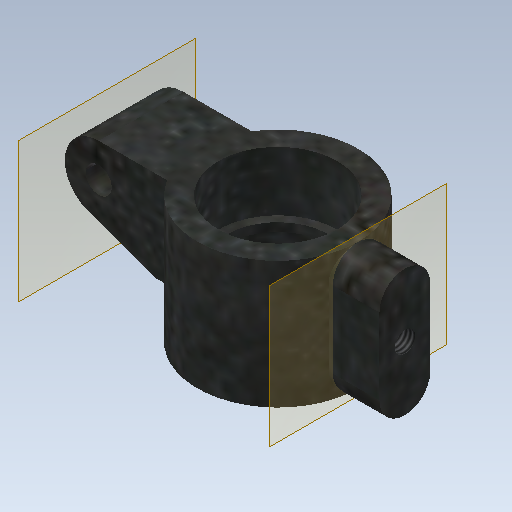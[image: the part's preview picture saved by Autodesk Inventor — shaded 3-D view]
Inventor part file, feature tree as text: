
AUTODESK INVENTOR PART (.ipt)
format: ipt  version: 2020 (Build 240168000, 168)  size: 269,824 bytes
history: native  units: mm
features: sketch x8, extrude x6, hole x3, plane x2, projected_geometry x1
ambient origin geometry x8: Origin, YZ Plane, XZ Plane, XY Plane, X Axis, Y Axis, Z Axis, Center Point
bodies: Solid1 (feature_tree)
feature tree (20):
  extrude  "Extrusion1"  Depth=15.0mm TaperAngle=0.0deg
  extrude  "Extrusion2"  Depth=7.0mm TaperAngle=0.0deg
  extrude  "Extrusion3"  Depth=7.0mm TaperAngle=0.0deg
  extrude  "Extrusion4"  Depth=21.5mm TaperAngle=0.0deg
  plane  "Work Plane1"
  extrude  "Extrusion5"  Depth=5.5mm TaperAngle=0.0deg
  extrude  "Extrusion6"  Depth=4.0mm
  hole  "Hole1"  [1 undecoded]
  hole  "Hole2"  [1 undecoded]
  plane  "Work Plane2"
  hole  "Hole3"  [1 undecoded]
  sketch  "Sketch1"  dims[d0=19.0mm d1=15.0mm d2=0.0mm]
  sketch  "Sketch2"  dims[d3=14.0mm d4=7.0mm d5=0.0mm]
  sketch  "Sketch3"  dims[d6=14.0mm d7=7.0mm d8=0.0mm]
  sketch  "Sketch5"  dims[d9=12.0mm d10=21.5mm d11=0.0mm]
  sketch  "Sketch6"  dims[d13=3.0mm d14=5.5mm d15=0.0mm]
  sketch  "Sketch7"  dims[d16=1.25mm d17=0.0mm d18=4.0mm]
  sketch  "Sketch8"  dims[d19=3.490659mm d21=16.15mm]
  sketch  "Sketch9"  dims[d22=10.0mm d23=0.0mm d49=10.0mm d50=10.0mm d26=3.1mm d27=6.0mm d28=4.0mm d29=2.0mm d30=90.0deg d31=17.3mm d32=20.594885mm d33=2.459mm d34=4.0mm d35=4.0mm d36=2.0mm d37=90.0deg d38=6.0mm d39=20.594885mm d40=2.459mm d41=4.0mm d42=4.0mm d43=2.0mm d44=90.0deg d45=4.0mm d46=20.594885mm]
  projected_geometry  "Project Cut Edges1"
note: 3 required parameter values undecoded (feature->parameter linkage not recoverable at this tier; creation-order binding heuristic only, values carry confidence <= 0.55)
